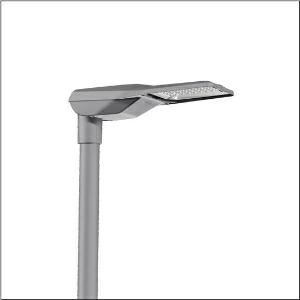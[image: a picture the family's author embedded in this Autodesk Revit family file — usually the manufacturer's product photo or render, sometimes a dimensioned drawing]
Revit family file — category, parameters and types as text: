
# Revit family: streetlight_sl_21_mini___st1_0a_5xe6d23a08hb_20ef
name_source: partatom
category: Lighting Fixtures
units: mm (PartAtom-declared; Revit-internal decimal feet)

## family parameters
Cut with Voids When Loaded = No
Host = Face
Light Source = No
Part Type = Normal
Room Calculation Point = No
Round Connector Dimension = Use Diameter
Shared = No

## types (1)
- --- (1 x LED, 7490 lm, 66 W, 2200K)
    Apparent Load = 66 VA
    CIE Flux Codes = 37 72 97 100 100
    Color Rendering = 70
    Color Temperature = 2200K
    Default Elevation = 1800 mm
    Description = Streetlight SL 21 mini, mast luminaire, primary light control with lens, of PMMA, primary optical cover: cover, of toughened safety glass, transparent, light distribution: ST1.0a, light emission: direct distribution, primary light characteristic: asymmetric, installation type: post-top, side-entry, LED, 3G 1.5mm², High Power LED, rated luminous flux: 7.490lm, luminous efficacy: 114lm/W, light colour: 722, colour temperature: 2200K, control: overheat protection, constant luminous flux control, time-dependent luminous flux control, flexible luminous flux parameterisation, mains connection: 230..240V, AC, 50/60Hz, connection cable pre-assembled, cable length: 8,5m, wiring characteristics: H07RN-F, start of lifetime: 66W, end of service life: 69W, reduction: 30W, luminaire housing, of diecast aluminium, powder-coated, Siteco® metallic grey (DB 702S), corrosivity category C5 mid according to DIN EN ISO 12944, please order mast flange separately, inclination adjustable: 0°, 5°, 10°, 15°, sealing non-destructively replaceable, multi-level sealing system, length: 628mm, width: 235mm, height: 110mm, mast flange for spigot size: 42mm (side-entry): 5XC10008XM4, 60/48mm (side-entry/post-top): 5XC10108XM2, 76/60mm (side-entry/post-top): 5XC10108XM1, protection rating (complete): IP66, insulation class (complete): insulation class II (safety insulation), certification: CE, ENEC, ENEC+, VDE, impact resistance: IK09, permissible operating ambient temperature for outdoor applications: -40..+50°C, standard-compliant lighting for roads and squares, packaging unit: 1 piece

Light Distribution: ST1.0a
    Height = 110 mm
    Lamp = 1 x LED
    Lamp Light Flux = 7490 lm
    Lamp Power = 66 W
    Lamp count = 1
    Length = 625 mm
    Luminous efficacy = 113 lm/W
    Manufacturer = Siteco
    ModVariant = No
    Model = 5XE6D23A08HB
    Number of Poles = 1
    OnlyDefault = Yes
    Power Factor = 1
    Product Name = Streetlight SL 21 mini | ST1.0a
    Product group = mast luminaire | pylon top
    ProductGroupID = 6100
    Protection Class = Protection class II
    Protection Degree = IP 66
    RLX_Detail_Level = 1
    RLX_Emergency_Light_Flux = 0 lm
    RLX_Emergency_Type = 0
    RLX_Emergency_Type_DB = No
    RlxData = <blob elided: 92321 chars, md5=ac18e849>
    Socket = socket
    Standby Power = 0 W
    System Light Flux = 7490 lm
    System Power = 66 W
    Type Comments = factory setting: luminous flux: 100 % | Output Level: 100 % | 670 mA
    Type Image = l_1003519.jpg
    URL = http://relux.com
    VarID = @adj_140347
    Voltage = 0 V
    Weight = 0.00 kg
    Width = 234 mm

## geometry (parser evidence)
native form markers: Blend x4, Sweep x11
no freeform markers — native parametric forms only
